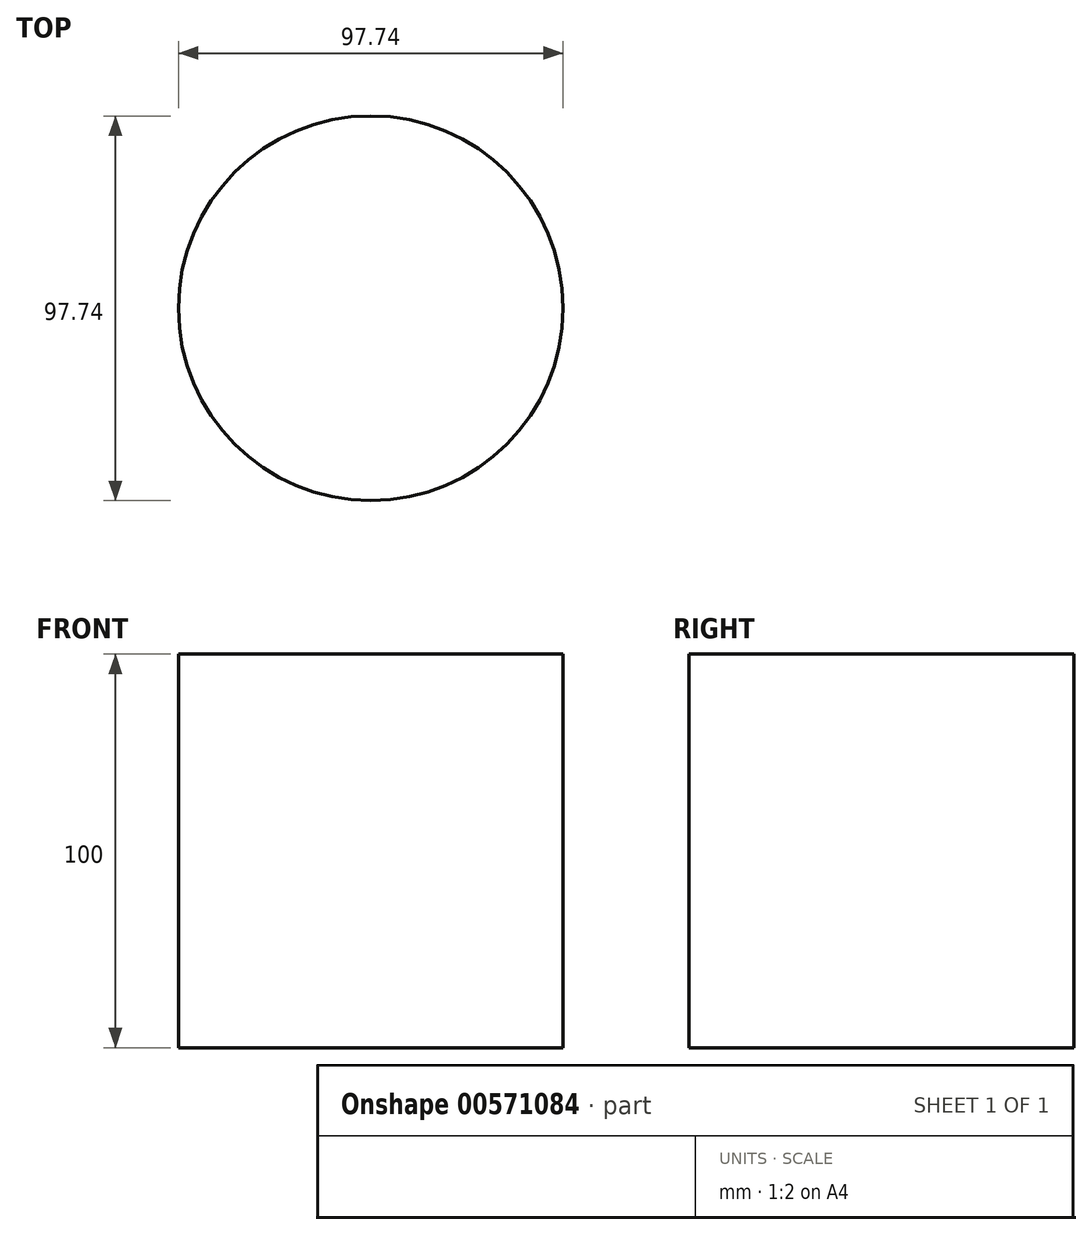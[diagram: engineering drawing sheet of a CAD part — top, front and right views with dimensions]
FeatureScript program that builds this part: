
annotation { "Feature Type Name" : "Feature", "Feature Type Description" : "" }
export const myFeature = defineFeature(function(context is Context, id is Id, definition is map)
    precondition{}
    {
        {
            var Q0;
            Q0=qCreatedBy(makeId("Top.planeOp"),FACE);
            var sketch = newSketch(context, id + "F0", { "sketchPlane" : qUnion([Q0])});
            skCircle(sketch, "E0", {"center": v(0, 0) * mm, "radius": 48.87 * mm});
            skSolve(sketch);
        }
        {
            var Q0;
            Q0=makeQuery(id+"F0.imprint","IMPRINT",FACE,{"disambiguationData":[TD([[makeQuery(id+"F0.imprint","IMPRINT",EDGE,{"derivedFrom":sQuery(id+"F0.wireOp",EDGE,"E0")}),1.0]])]});
            extrude(context, id + "F1", {"entities" : qUnion([Q0]), "depth" : 100 * mm, "offsetDistance" : 25.4 * mm});
        }
    });
